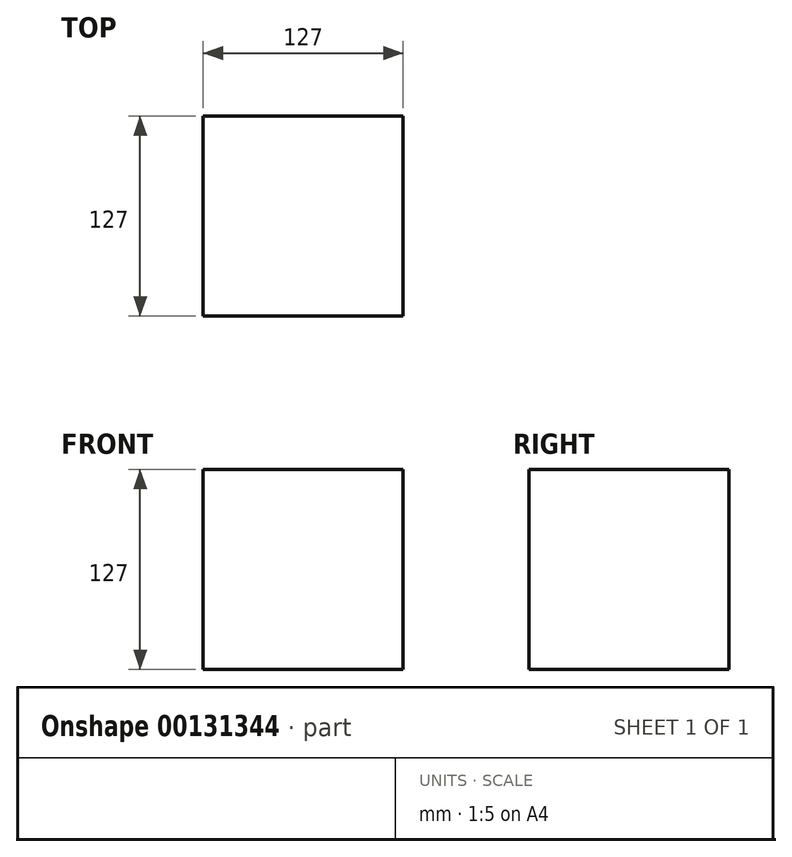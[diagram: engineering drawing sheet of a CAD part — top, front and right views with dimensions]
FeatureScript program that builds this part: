
annotation { "Feature Type Name" : "Feature", "Feature Type Description" : "" }
export const myFeature = defineFeature(function(context is Context, id is Id, definition is map)
    precondition{}
    {
        {
            var Q0;
            Q0=qCreatedBy(makeId("Front.planeOp"),FACE);
            var sketch = newSketch(context, id + "F0", { "sketchPlane" : qUnion([Q0])});
            skLineSegment(sketch, "E0.bottom", {"start": v(63.5, -63.5) * mm, "end": v(-63.5, -63.5) * mm});
            skLineSegment(sketch, "E0.top", {"start": v(63.5, 63.5) * mm, "end": v(-63.5, 63.5) * mm});
            skLineSegment(sketch, "E0.left", {"start": v(63.5, -63.5) * mm, "end": v(63.5, 63.5) * mm});
            skLineSegment(sketch, "E0.right", {"start": v(-63.5, -63.5) * mm, "end": v(-63.5, 63.5) * mm});
            skPoint(sketch, "E0.middle", {"position": v(0, 0) * mm});
            skSolve(sketch);
        }
        {
            var Q0;
            Q0 = qSketchRegion(id + "F0", true);
            extrude(context, id + "F1", {"entities" : qUnion([Q0]), "depth" : 127 * mm});
        }
    });
